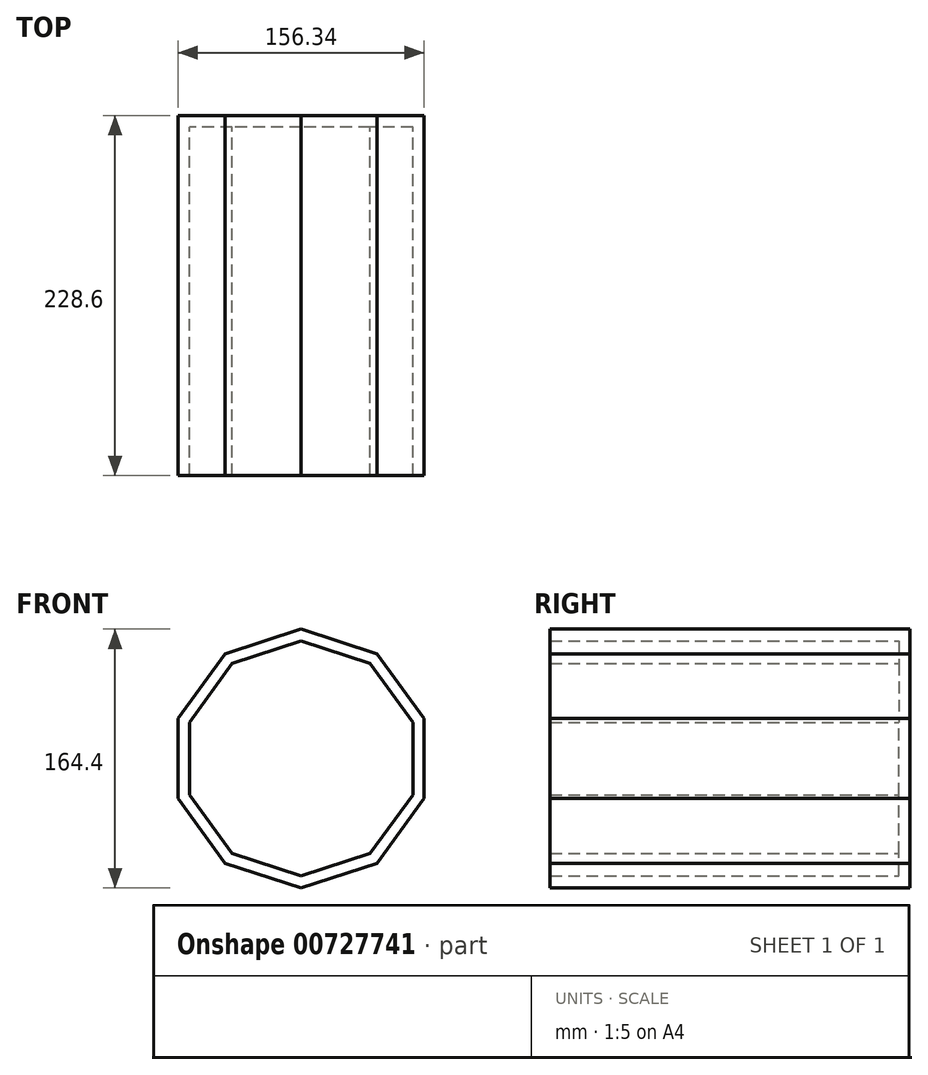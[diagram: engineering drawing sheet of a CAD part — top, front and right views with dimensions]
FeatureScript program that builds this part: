
annotation { "Feature Type Name" : "Feature", "Feature Type Description" : "" }
export const myFeature = defineFeature(function(context is Context, id is Id, definition is map)
    precondition{}
    {
        {
            var Q0;
            Q0=qCreatedBy(makeId("Front.planeOp"),FACE);
            var sketch = newSketch(context, id + "F0", { "sketchPlane" : qUnion([Q0])});
            skCircle(sketch, "E0.cCircle", {"center": v(3.53, 0) * mm, "radius": 78.17 * mm, "construction": true});
            skLineSegment(sketch, "E0.0", {"start": v(-74.64, -25.4) * mm, "end": v(-74.64, 25.4) * mm});
            skLineSegment(sketch, "E0.1", {"start": v(-74.64, 25.4) * mm, "end": v(-44.78, 66.5) * mm});
            skLineSegment(sketch, "E0.2", {"start": v(-44.78, 66.5) * mm, "end": v(3.53, 82.2) * mm});
            skLineSegment(sketch, "E0.3", {"start": v(3.53, 82.2) * mm, "end": v(51.84, 66.5) * mm});
            skLineSegment(sketch, "E0.4", {"start": v(51.84, 66.5) * mm, "end": v(81.7, 25.4) * mm});
            skLineSegment(sketch, "E0.5", {"start": v(81.7, 25.4) * mm, "end": v(81.7, -25.4) * mm});
            skLineSegment(sketch, "E0.6", {"start": v(81.7, -25.4) * mm, "end": v(51.84, -66.5) * mm});
            skLineSegment(sketch, "E0.7", {"start": v(51.84, -66.5) * mm, "end": v(3.53, -82.2) * mm});
            skLineSegment(sketch, "E0.8", {"start": v(3.53, -82.2) * mm, "end": v(-44.78, -66.5) * mm});
            skLineSegment(sketch, "E0.9", {"start": v(-44.78, -66.5) * mm, "end": v(-74.64, -25.4) * mm});
            skPoint(sketch, "E0.0.midPoint", {"position": v(-74.64, 0) * mm});
            skSolve(sketch);
        }
        {
            var Q0;
            Q0 = qSketchRegion(id + "F0", true);
            extrude(context, id + "F1", {"entities" : qUnion([Q0]), "depth" : 228.6 * mm, "offsetDistance" : 25.4 * mm});
        }
        {
            var Q0;
            Q0=makeQuery(id+"F1.opExtrude","CAP_FACE",FACE,{"disambiguationData":[OSD([sQuery(id+"F0.wireOp",EDGE,"E0.0"),sQuery(id+"F0.wireOp",EDGE,"E0.1"),sQuery(id+"F0.wireOp",EDGE,"E0.2"),sQuery(id+"F0.wireOp",EDGE,"E0.3"),sQuery(id+"F0.wireOp",EDGE,"E0.4"),sQuery(id+"F0.wireOp",EDGE,"E0.5"),sQuery(id+"F0.wireOp",EDGE,"E0.6"),sQuery(id+"F0.wireOp",EDGE,"E0.7"),sQuery(id+"F0.wireOp",EDGE,"E0.8"),sQuery(id+"F0.wireOp",EDGE,"E0.9")])],"isStart":false});
            shell(context, id + "F2", {"entities" : qUnion([Q0]), "thickness" : 7.26 * mm});
        }
    });
